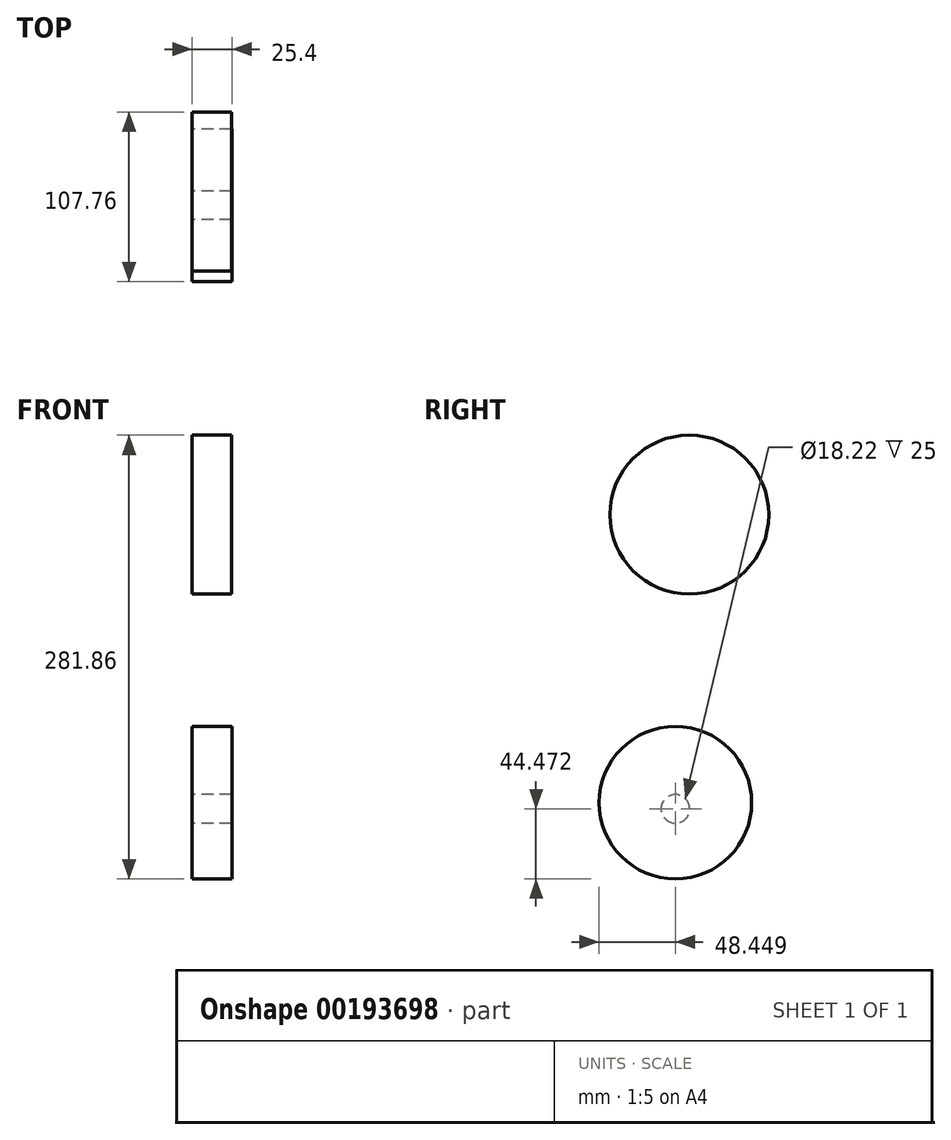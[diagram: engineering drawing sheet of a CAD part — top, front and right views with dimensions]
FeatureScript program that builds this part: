
annotation { "Feature Type Name" : "Feature", "Feature Type Description" : "" }
export const myFeature = defineFeature(function(context is Context, id is Id, definition is map)
    precondition{}
    {
        {
            var Q0;
            Q0=qCreatedBy(makeId("Right.planeOp"),FACE);
            var sketch = newSketch(context, id + "F0", { "sketchPlane" : qUnion([Q0])});
            skCircle(sketch, "E0", {"center": v(-33.8, -110.02) * mm, "radius": 48.44 * mm});
            skSolve(sketch);
        }
        {
            var Q0;
            Q0=qCreatedBy(makeId("Right.planeOp"),FACE);
            var sketch = newSketch(context, id + "F1", { "sketchPlane" : qUnion([Q0])});
            skCircle(sketch, "E1", {"center": v(-24.96, 72.92) * mm, "radius": 50.47 * mm});
            skSolve(sketch);
        }
        {
            var Q0;
            Q0=makeQuery(id+"F0.imprint","IMPRINT",FACE,{"disambiguationData":[TD([[makeQuery(id+"F0.imprint","IMPRINT",EDGE,{"derivedFrom":sQuery(id+"F0.wireOp",EDGE,"E0")}),1.0]])]});
            extrude(context, id + "F2", {"entities" : qUnion([Q0]), "depth" : 25.4 * mm});
        }
        {
            var Q0;
            Q0=makeQuery(id+"F1.imprint","IMPRINT",FACE,{"disambiguationData":[TD([[makeQuery(id+"F1.imprint","IMPRINT",EDGE,{"derivedFrom":sQuery(id+"F1.wireOp",EDGE,"E1")}),1.0]])]});
            extrude(context, id + "F3", {"entities" : qUnion([Q0]), "depth" : 25 * mm});
        }
        {
            var Q0;
            Q0=makeQuery(id+"F2.opExtrude","CAP_FACE",FACE,{"disambiguationData":[OSD([sQuery(id+"F0.wireOp",EDGE,"E0")])],"isStart":true});
            var sketch = newSketch(context, id + "F4", { "sketchPlane" : qUnion([Q0])});
            skCircle(sketch, "E2", {"center": v(33.8, -114) * mm, "radius": 9.1 * mm});
            skSolve(sketch);
        }
        {
            var Q0;
            Q0=makeQuery(id+"F4.imprint","IMPRINT",FACE,{"disambiguationData":[TD([[makeQuery(id+"F4.imprint","IMPRINT",EDGE,{"derivedFrom":sQuery(id+"F4.wireOp",EDGE,"E2")}),1.0]])]});
            extrude(context, id + "F5", {"entities" : qUnion([Q0]), "operationType" : NewBodyOperationType.REMOVE, "oppositeDirection" : true, "depth" : 25 * mm});
        }
    });
